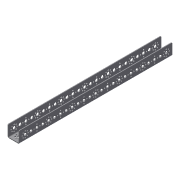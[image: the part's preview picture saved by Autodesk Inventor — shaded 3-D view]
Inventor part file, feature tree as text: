
AUTODESK INVENTOR PART (.ipt)
format: ipt  version: 2013 (Build 170138000, 138)  size: 499,712 bytes
history: native  units: mm
features: hole x28, other x5, sheet_metal_op x4, sketch x3, extrude x1, fillet x1
ambient origin geometry x8: Origin, YZ Plane, XZ Plane, XY Plane, X Axis, Y Axis, Z Axis, Center Point
bodies: Solid1 (feature_tree)
feature tree (42):
  other  "Blocks"
  sheet_metal_op  "Face1"
  sheet_metal_op  "Flange1"
  extrude  "Extrusion1"  Depth=416.0mm
  fillet  "Fillet1"  Radius=16.0mm
  sketch  "Sketch1"  dims[d0=32.0mm d1=416.0mm d3=16.0mm d4=3.7mm]
  hole  "Hole Pattern 4"  [1 undecoded]
  hole  "Hole Pattern 8"  [1 undecoded]
  other  "Plate1"
  sketch  "Sketch2"  dims[d6=16.0mm d8=16.0mm]
  other  "Plate2"
  sheet_metal_op  "Bend1"
  sheet_metal_op  "Corner1"
  sketch  "Sketch3"  dims[d9=16.0mm d10=8.0mm d13=3.7mm d14=8.0mm d15=80.0mm d17=360.0deg d20=16.0mm d21=16.0mm d22=16.0mm d23=16.0mm d25=16.0mm d26=16.0mm d27=2.0mm d28=2.0mm d29=1.0mm d30=4.0mm d31=2.0mm d32=32.0mm d33=90.0deg d34=2.0mm d35=8.0mm d36=2.0mm d37=2.0mm d38=16.0mm d39=16.0mm d40=16.0mm d41=16.0mm d42=16.0mm d43=16.0mm d45=16.0mm d46=10.0mm d47=0.0mm d48=2.0mm]
  other  "416 mm hole pattern"
  hole  "Hole Pattern 4:1"  [1 undecoded]
  hole  "Hole Pattern 8:1"  [1 undecoded]
  hole  "Hole Pattern 8:2"  [1 undecoded]
  hole  "Hole Pattern 4:2"  [1 undecoded]
  hole  "Hole Pattern 8:3"  [1 undecoded]
  hole  "Hole Pattern 4:3"  [1 undecoded]
  hole  "Hole Pattern 8:4"  [1 undecoded]
  hole  "Hole Pattern 4:4"  [1 undecoded]
  hole  "Hole Pattern 8:5"  [1 undecoded]
  hole  "Hole Pattern 8:6"  [1 undecoded]
  hole  "Hole Pattern 4:5"  [1 undecoded]
  hole  "Hole Pattern 8:7"  [1 undecoded]
  hole  "Hole Pattern 4:6"  [1 undecoded]
  other  "416 mm hole pattern:1"
  hole  "Hole Pattern 4:13"  [1 undecoded]
  hole  "Hole Pattern 8:15"  [1 undecoded]
  hole  "Hole Pattern 8:16"  [1 undecoded]
  hole  "Hole Pattern 4:14"  [1 undecoded]
  hole  "Hole Pattern 8:17"  [1 undecoded]
  hole  "Hole Pattern 4:15"  [1 undecoded]
  hole  "Hole Pattern 8:18"  [1 undecoded]
  hole  "Hole Pattern 4:16"  [1 undecoded]
  hole  "Hole Pattern 8:19"  [1 undecoded]
  hole  "Hole Pattern 8:20"  [1 undecoded]
  hole  "Hole Pattern 4:17"  [1 undecoded]
  hole  "Hole Pattern 8:21"  [1 undecoded]
  hole  "Hole Pattern 4:18"  [1 undecoded]
note: 28 required parameter values undecoded (feature->parameter linkage not recoverable at this tier; creation-order binding heuristic only, values carry confidence <= 0.55)
